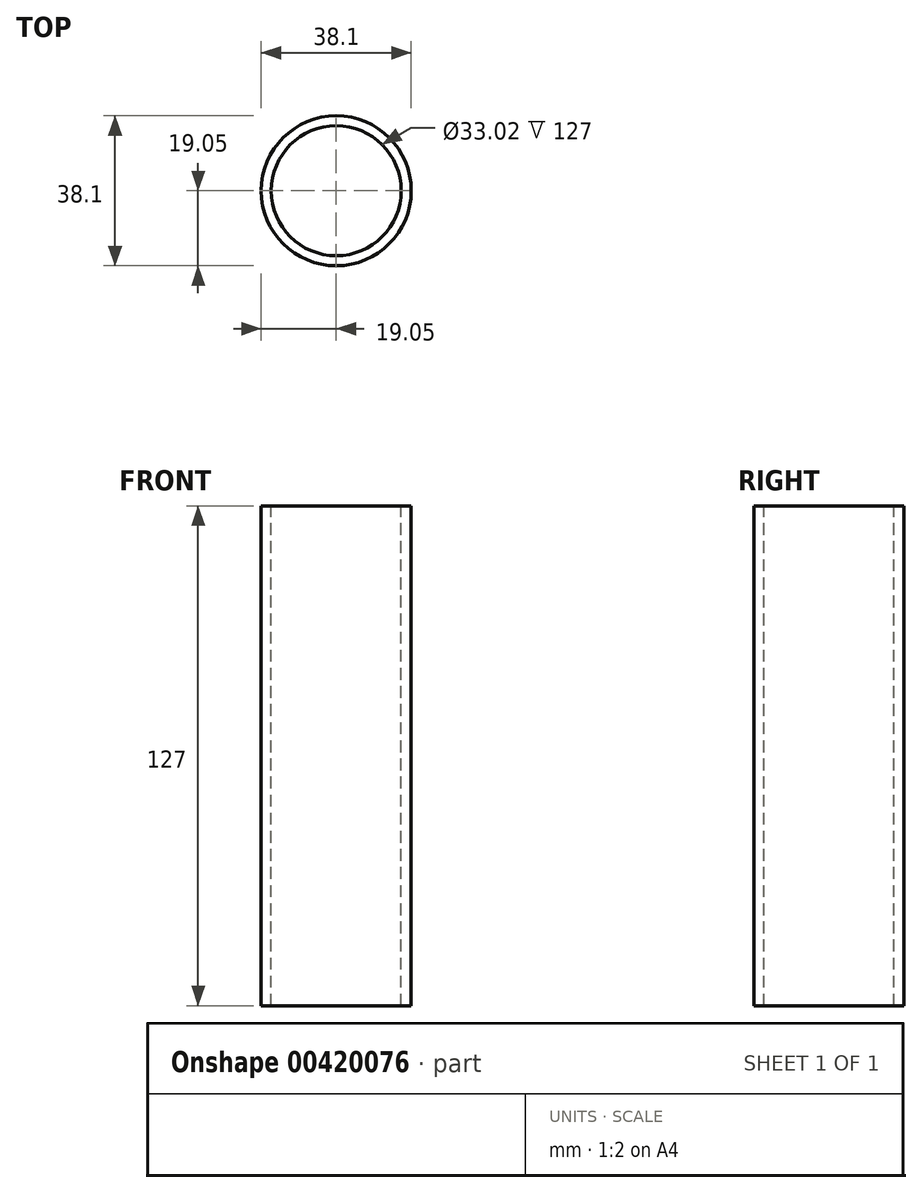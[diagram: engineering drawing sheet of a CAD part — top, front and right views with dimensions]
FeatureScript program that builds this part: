
annotation { "Feature Type Name" : "Feature", "Feature Type Description" : "" }
export const myFeature = defineFeature(function(context is Context, id is Id, definition is map)
    precondition{}
    {
        {
            var Q0;
            Q0=qCreatedBy(makeId("Top.planeOp"),FACE);
            var sketch = newSketch(context, id + "F0", { "sketchPlane" : qUnion([Q0])});
            skCircle(sketch, "E0", {"center": v(0, 0) * mm, "radius": 16.51 * mm});
            skCircle(sketch, "E1", {"center": v(0, 0) * mm, "radius": 19.05 * mm});
            skSolve(sketch);
        }
        {
            var Q0;
            Q0=makeQuery(id+"F0.imprint","IMPRINT",FACE,{"disambiguationData":[TD([[makeQuery(id+"F0.imprint","IMPRINT",EDGE,{"derivedFrom":sQuery(id+"F0.wireOp",EDGE,"E0")}),-1.0]])]});
            extrude(context, id + "F1", {"entities" : qUnion([Q0]), "oppositeDirection" : true, "depth" : 127 * mm});
        }
    });
